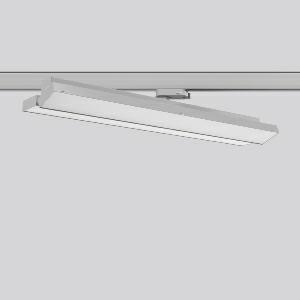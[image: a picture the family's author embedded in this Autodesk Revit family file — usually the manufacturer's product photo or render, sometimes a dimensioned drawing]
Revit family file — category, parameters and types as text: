
# Revit family: tx-move_742164_004_3_3688
name_source: partatom
category: Lighting Fixtures
units: mm (PartAtom-declared; Revit-internal decimal feet)

## family parameters
Cut with Voids When Loaded = No
Host = Face
Light Source = No
Part Type = Normal
Room Calculation Point = No
Round Connector Dimension = Use Diameter
Shared = No

## types (1)
- MultiLumen 1 (1 x LED Modul 835, 2550 lm, 3500)
    Apparent Load = 41 VA
    CIE Flux Codes = 47 79 96 100 100
    Color Rendering = 80
    Color Temperature = 3500
    Default Elevation = 1800 mm
    Description = Series: TX-MOVE
Multifunctional surface-mounted spotlight for area lighting. Very flat design. Housing: sheet steel, powder-coated. Rotation range: 356°. Swivel range: 90°. Consistent alignment possible with visible tilt scale. High-efficiency LED units with flush-mounted opal diffuser made of non-yellowing PMMA. Symmetrical wide beam light emission. With multi adaptor for 3-circuit tracks 230 V. Suitable for Track on ceiling. MultiLumen: Luminous flux adjustable in 3 steps. Factory setting is the highest luminous flux. Environmentally friendly and resource-saving due to replaceable and recyclable components. 
Colour: silver, matt (approx. RAL 9006)
Length: 570 mm
Width: 119 mm
Height: 92 mm
Lamp: LED
Socket: without socket
Colour temperature: 3500K
Colour rendering index (CRI): 80
System power: 41 W
Rated luminous flux: 5100 lm
Luminous efficiency: 124 lm/W
System power 2: 57 W
Rated luminous flux 2: 6950 lm
Luminous efficiency 2: 122 lm/W
System power 3: 73 W
Rated luminous flux 3: 8500 lm
Luminous efficiency 3: 116 lm/W
Control gear: Regulated power supply
Protection class: I
Type of protection: IP 20
    Height = 75 mm
    Lamp = 1 x LED Modul 835
    Lamp Light Flux = 2550 lm
    Lamp count = 1
    Length = 569 mm
    Lifetime = 50000 h
    Luminous efficacy = 124 lm/W
    Manufacturer = RZB
    ModVariant = No
    Model = 742164.004.3
    Mounting Place = Ceiling
    Mounting Type = Rail mounted
    Number of Poles = 1
    OnlyDefault = Yes
    Power Factor = 1
    Product Name = TX-MOVE
    Product group = Track mounted projectors
    ProductGroupID = 301
    Protection Class = Protection class I
    Protection Degree = IP 20
    RLX_Detail_Level = 1
    RLX_Emergency_Light_Flux = 0 lm
    RLX_Emergency_Type = 0
    RLX_Emergency_Type_DB = No
    RlxData = <blob elided: 32197 chars, md5=0c3b76ba>
    Socket = socket
    Standby Power = 0 W
    System Light Flux = 5100 lm
    System Power = 41 W
    Type Comments = MultiLumen 1
    Type Image = 742164.004.jpg
    URL = http://relux.com
    VarID = multilumen_1
    Voltage = 230 V
    Voltage Range = 220-240 V
    Weight = 0.00 kg
    Width = 119 mm

## geometry (parser evidence)
native form markers: Blend x4, Sweep x13
no freeform markers — native parametric forms only
